# Revit family: BuroSeating_Konfurb Orbit HB_5 Star
name_source: partatom
category: Furniture
units: mm (PartAtom-declared; Revit-internal decimal feet)

## family parameters
Always vertical = Yes
Cut with Voids When Loaded = No
OmniClass Number = 23.40.70.14.64.11
OmniClass Title = Office Furniture
Room Calculation Point = No
Shared = Yes
Work Plane-Based = No

## types (1)
- Konfurb Orbit 5 Star Swivel High Back
    Assembly Code = E2020
    BaseMaterial = BuroSeating_Aluminium_Black
    BottomLiftMaterial = BuroSeating_Aluminium_Black
    CastorMaterial = BuroSeating_Aluminium_Black
    CastorWheelMaterial = BuroSeating_Plastic_Black
    Default Elevation = 0 mm  [stored 0 ft]
    Description = Konfurb Orbit 5 Star Swivel High Back
    Manufacturer = Buro Seating
    Model = KON184
    NominalArmHeight = 590-690h
    NominalChairHeight = 1270-1370h
    NominalDepth = 600 mm  [stored 1.9685 ft]
    NominalSeatHeight = 420-520h
    NominalWidth = 650 mm  [stored 2.13255 ft]
    ProductGroup = Orbit
    ProductPageURL AU = https://buroseating.com
    ProductPageURL NZ = https://buroseating.co.nz
    ProductRange = Buro
    SeatArms = No
    SeatBackHeght = 840 mm  [stored 2.75591 ft]
    SeatDepth = 470 mm  [stored 1.54199 ft]
    SeatHeadRest = No
    SeatLeverHandleMaterial = BuroSeating_Aluminium_Black
    SeatTiltMaterial = BuroSeating_Aluminium_Black
    SeatWidth = 515 mm  [stored 1.68963 ft]
    TopLiftMaterial = BuroSeating_Metal_Chrome_Semi-Polished
    Type Comments = Seat Height 420-520mm High
    URL = https://buroseating.co.nz
    URL AU = https://buroseating.com
    WarrantyDescription = Full 5 year guarantee (excluding upholstery)

note: [stored X ft] marks values corroborated as IEEE doubles in the binary element streams (Revit-internal decimal feet)

## geometry (parser evidence)
native form markers: Sweep x8
no freeform markers — native parametric forms only
